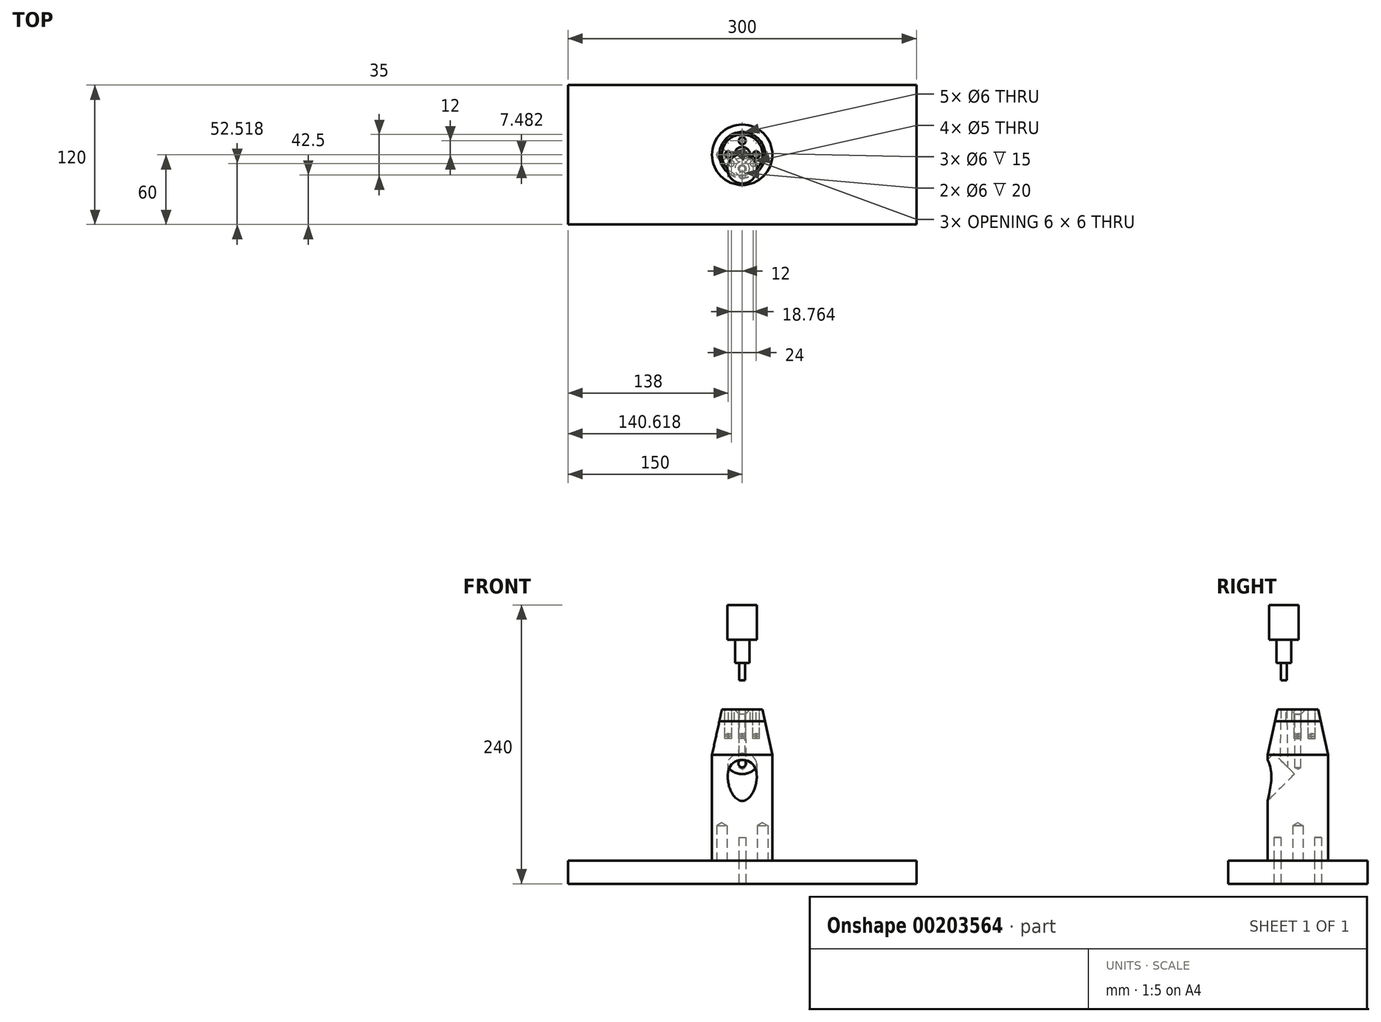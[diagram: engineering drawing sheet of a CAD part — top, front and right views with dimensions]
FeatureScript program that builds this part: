
annotation { "Feature Type Name" : "Feature", "Feature Type Description" : "" }
export const myFeature = defineFeature(function(context is Context, id is Id, definition is map)
    precondition{}
    {
        {
            var Q0;
            Q0=qCreatedBy(makeId("Front.planeOp"),FACE);
            var sketch = newSketch(context, id + "F0", { "sketchPlane" : qUnion([Q0])});
            skLineSegment(sketch, "E0", {"start": v(0, 0) * mm, "end": v(17.5, 0) * mm, "construction": true});
            skLineSegment(sketch, "E1", {"start": v(17.5, 0) * mm, "end": v(26, -39.09) * mm, "construction": true});
            skLineSegment(sketch, "E2", {"start": v(26, -39.09) * mm, "end": v(0, -39.09) * mm, "construction": true});
            skLineSegment(sketch, "E3", {"start": v(0, -10) * mm, "end": v(19.67, -10) * mm});
            skLineSegment(sketch, "E4", {"start": v(19.67, -10) * mm, "end": v(26, -39.09) * mm});
            skLineSegment(sketch, "E5", {"start": v(26, -130) * mm, "end": v(0, -130) * mm});
            skLineSegment(sketch, "E6", {"start": v(26, -39.09) * mm, "end": v(26, -130) * mm});
            skLineSegment(sketch, "E7", {"start": v(0, -130) * mm, "end": v(0, -10) * mm});
            skSolve(sketch);
        }
        {
            var Q0;
            Q0 = qSketchRegion(id + "F0", true);
            var Q1;
            Q1=sQuery(id+"F0.wireOp",EDGE,"E7");
            revolve(context, id + "F1", {"entities" : qUnion([Q0]), "axis" : qUnion([Q1]), "revolveType" : RevolveType.FULL});
        }
        {
            var Q0;
            Q0=qCreatedBy(makeId("Front.planeOp"),FACE);
            var sketch = newSketch(context, id + "F2", { "sketchPlane" : qUnion([Q0])});
            skPoint(sketch, "E8.0", {"position": v(0, 0) * mm});
            skLineSegment(sketch, "E9.0", {"start": v(0, 0) * mm, "end": v(17.5, 0) * mm});
            skLineSegment(sketch, "E10.0", {"start": v(17.5, 0) * mm, "end": v(19.67, -10) * mm});
            skLineSegment(sketch, "E11.0", {"start": v(0, -10) * mm, "end": v(19.67, -10) * mm});
            skLineSegment(sketch, "E12", {"start": v(0, -10) * mm, "end": v(0, 0) * mm});
            skPoint(sketch, "E13.orphan", {"position": v(26, -39.09) * mm});
            skSolve(sketch);
        }
        {
            var Q0;
            Q0 = qSketchRegion(id + "F2", true);
            var Q1;
            Q1=sQuery(id+"F2.wireOp",EDGE,"E12");
            revolve(context, id + "F3", {"entities" : qUnion([Q0]), "axis" : qUnion([Q1]), "revolveType" : RevolveType.FULL});
        }
        {
            var Q0;
            Q0=makeQuery(id+"F3.opRevolve","SWEPT_FACE",FACE,{"disambiguationData":[OSD([sQuery(id+"F2.wireOp",EDGE,"E9.0")])]});
            var sketch = newSketch(context, id + "F4", { "sketchPlane" : qUnion([Q0])});
            skCircle(sketch, "E14", {"center": v(0, 0) * mm, "radius": 12 * mm, "construction": true});
            skLineSegment(sketch, "E15", {"start": v(0, 0) * mm, "end": v(0, -17.5) * mm, "construction": true});
            skCircle(sketch, "E16", {"center": v(0, -12) * mm, "radius": 2.5 * mm});
            skSolve(sketch);
        }
        {
            var Q0;
            Q0 = qSketchRegion(id + "F4", true);
            extrude(context, id + "F5", {"entities" : qUnion([Q0]), "operationType" : NewBodyOperationType.REMOVE, "oppositeDirection" : true, "depth" : 50 * mm, "hasDraft" : true, "draftAngle" : 1 * degree});
        }
        {
            var Q0;
            Q0=makeQuery(id+"F3.opRevolve","SWEPT_FACE",FACE,{"disambiguationData":[OSD([sQuery(id+"F2.wireOp",EDGE,"E9.0")])]});
            var sketch = newSketch(context, id + "F6", { "sketchPlane" : qUnion([Q0])});
            skCircle(sketch, "E17.0", {"center": v(0, 0) * mm, "radius": 12 * mm, "construction": true});
            skLineSegment(sketch, "E18.0", {"start": v(0, 0) * mm, "end": v(0, -17.5) * mm, "construction": true});
            skLineSegment(sketch, "E19", {"start": v(0, 0) * mm, "end": v(-13.68, -10.91) * mm, "construction": true});
            skLineSegment(sketch, "E20", {"start": v(0, 0) * mm, "end": v(13.68, -10.91) * mm, "construction": true});
            skCircle(sketch, "E21", {"center": v(-9.38, -7.48) * mm, "radius": 2.5 * mm});
            skCircle(sketch, "E22", {"center": v(9.38, -7.48) * mm, "radius": 2.5 * mm});
            skSolve(sketch);
        }
        {
            var Q0;
            Q0 = qSketchRegion(id + "F6", true);
            extrude(context, id + "F7", {"entities" : qUnion([Q0]), "operationType" : NewBodyOperationType.REMOVE, "endBound" : BoundingType.UP_TO_NEXT, "oppositeDirection" : true, "depth" : 25 * mm});
        }
        {
            var Q0;
            Q0=makeQuery(id+"F4.imprint","IMPRINT",FACE,{"disambiguationData":[TD([[makeQuery(id+"F4.imprint","IMPRINT",EDGE,{"derivedFrom":sQuery(id+"F4.wireOp",EDGE,"E16")}),-1.0]])]});
            var sketch = newSketch(context, id + "F8", { "sketchPlane" : qUnion([Q0])});
            skCircle(sketch, "E23.0", {"center": v(0, 0) * mm, "radius": 12 * mm, "construction": true});
            skLineSegment(sketch, "E24", {"start": v(-17.5, 0) * mm, "end": v(17.5, 0) * mm, "construction": true});
            skCircle(sketch, "E25", {"center": v(-12, 0) * mm, "radius": 3 * mm});
            skCircle(sketch, "E26", {"center": v(12, 0) * mm, "radius": 3 * mm});
            skCircle(sketch, "E27", {"center": v(0, 12) * mm, "radius": 3 * mm});
            skSolve(sketch);
        }
        {
            var Q0;
            Q0 = qSketchRegion(id + "F8", true);
            extrude(context, id + "F9", {"entities" : qUnion([Q0]), "operationType" : NewBodyOperationType.REMOVE, "oppositeDirection" : true, "depth" : 25 * mm});
        }
        {
            var Q0;
            Q0 = qSketchRegion(id + "F8", true);
            extrude(context, id + "F10", {"entities" : qUnion([Q0]), "oppositeDirection" : true, "depth" : 25 * mm});
        }
        {
            var Q0;
            Q0=makeQuery(id+"F10.opExtrude","CAP_EDGE",EDGE,{"disambiguationData":[OSD([sQuery(id+"F8.wireOp",EDGE,"E25")])],"isStart":true});
            var Q1;
            Q1=makeQuery(id+"F10.opExtrude","CAP_EDGE",EDGE,{"disambiguationData":[OSD([sQuery(id+"F8.wireOp",EDGE,"E27")])],"isStart":true});
            var Q2;
            Q2=makeQuery(id+"F10.opExtrude","CAP_EDGE",EDGE,{"disambiguationData":[OSD([sQuery(id+"F8.wireOp",EDGE,"E26")])],"isStart":true});
            var Q3;
            Q3=makeQuery(id+"F10.opExtrude","CAP_EDGE",EDGE,{"disambiguationData":[OSD([sQuery(id+"F8.wireOp",EDGE,"E27")])],"isStart":false});
            var Q4;
            Q4=makeQuery(id+"F10.opExtrude","CAP_EDGE",EDGE,{"disambiguationData":[OSD([sQuery(id+"F8.wireOp",EDGE,"E25")])],"isStart":false});
            var Q5;
            Q5=makeQuery(id+"F10.opExtrude","CAP_EDGE",EDGE,{"disambiguationData":[OSD([sQuery(id+"F8.wireOp",EDGE,"E26")])],"isStart":false});
            fillet(context, id + "F11", {"entities" : qUnion([Q0, Q1, Q2, Q3, Q4, Q5]), "radius" : 2 * mm, "tangentPropagation" : true, "allowEdgeOverflow" : false});
        }
        {
            var Q0;
            Q0=sQuery(id+"F4.wireOp",VERTEX,"E14.center");
            var Q1;
            Q1=makeQuery(id+"F1.opRevolve","SWEPT_BODY",BODY,{"disambiguationData":[OSD([sQuery(id+"F0.wireOp",EDGE,"E3"),sQuery(id+"F0.wireOp",EDGE,"E4"),sQuery(id+"F0.wireOp",EDGE,"E5"),sQuery(id+"F0.wireOp",EDGE,"E6"),sQuery(id+"F0.wireOp",EDGE,"E7")])]});
            var Q2;
            Q2=makeQuery(id+"F3.opRevolve","SWEPT_BODY",BODY,{"disambiguationData":[OSD([sQuery(id+"F2.wireOp",EDGE,"E9.0"),sQuery(id+"F2.wireOp",EDGE,"E10.0"),sQuery(id+"F2.wireOp",EDGE,"E11.0"),sQuery(id+"F2.wireOp",EDGE,"E12")])]});
            hole(context, id + "F12", {"style" : HoleStyle.C_SINK, "endStyle" : HoleEndStyle.BLIND, "standardTappedOrClearance" : lookupTablePath({ "standard" : "ISO", "engagement" : "75%", "pitch" : "1 mm", "size" : "M6", "type" : "Tapped" }), "standardBlindInLast" : lookupTablePath({ "standard" : "ISO", "engagement" : "75%", "pitch" : "1 mm", "size" : "M6", "type" : "Tapped" }), "holeDiameter" : 5 * mm, "cSinkDiameter" : 13.44 * mm, "cSinkAngle" : 90 * degree, "holeDepth" : 50 * mm, "startFromSketch" : true, "locations" : qUnion([Q0]), "scope" : qUnion([Q1, Q2]), "majorDiameter" : 6 * mm});
        }
        {
            var Q0;
            Q0=qCreatedBy(makeId("Right.planeOp"),FACE);
            var sketch = newSketch(context, id + "F13", { "sketchPlane" : qUnion([Q0])});
            skLineSegment(sketch, "E28", {"start": v(0, -35) * mm, "end": v(-36.42, -71.42) * mm, "construction": true});
            skSolve(sketch);
        }
        {
            var Q0;
            Q0=sQuery(id+"F13.wireOp",EDGE,"E28");
            var Q1;
            Q1=sQuery(id+"F13.wireOp",VERTEX,"E28.end");
            cPlane(context, id + "F14", {"entities" : qUnion([Q0, Q1]), "cplaneType" : CPlaneType.LINE_POINT, "offset" : 25 * mm, "width" : 150 * mm, "height" : 150 * mm});
        }
        {
            var Q0;
            Q0=qCreatedBy(id+"F14.planeOp",FACE);
            var sketch = newSketch(context, id + "F15", { "sketchPlane" : qUnion([Q0])});
            skPoint(sketch, "E29.0", {"position": v(0, -24.75) * mm});
            skCircle(sketch, "E30", {"center": v(0, -24.75) * mm, "radius": 12.5 * mm});
            skSolve(sketch);
        }
        {
            var Q0;
            Q0 = qSketchRegion(id + "F15", true);
            extrude(context, id + "F16", {"entities" : qUnion([Q0]), "operationType" : NewBodyOperationType.REMOVE, "oppositeDirection" : true, "depth" : 35 * mm});
        }
        {
            var Q0;
            Q0=qCreatedBy(makeId("Top.planeOp"),FACE);
            cPlane(context, id + "F17", {"entities" : qUnion([Q0]), "cplaneType" : CPlaneType.OFFSET, "offset" : 25 * mm, "width" : 150 * mm, "height" : 150 * mm});
        }
        {
            var Q0;
            Q0=qCreatedBy(id+"F17.planeOp",FACE);
            var sketch = newSketch(context, id + "F18", { "sketchPlane" : qUnion([Q0])});
            skCircle(sketch, "E31.0", {"center": v(0, -12) * mm, "radius": 2.5 * mm});
            skSolve(sketch);
        }
        {
            var Q0;
            Q0 = qSketchRegion(id + "F18", true);
            extrude(context, id + "F19", {"entities" : qUnion([Q0]), "depth" : 15 * mm});
        }
        {
            var Q0;
            Q0=makeQuery(id+"F19.opExtrude","CAP_FACE",FACE,{"disambiguationData":[OSD([sQuery(id+"F18.wireOp",EDGE,"E31.0")])],"isStart":false});
            var sketch = newSketch(context, id + "F20", { "sketchPlane" : qUnion([Q0])});
            skCircle(sketch, "E32", {"center": v(0, -12) * mm, "radius": 6.25 * mm});
            skSolve(sketch);
        }
        {
            var Q0;
            Q0 = qSketchRegion(id + "F20", true);
            extrude(context, id + "F21", {"entities" : qUnion([Q0]), "operationType" : NewBodyOperationType.ADD, "depth" : 20 * mm});
        }
        {
            var Q0;
            Q0=makeQuery(id+"F21.opExtrude","CAP_FACE",FACE,{"disambiguationData":[OSD([sQuery(id+"F20.wireOp",EDGE,"E32")])],"isStart":false});
            var sketch = newSketch(context, id + "F22", { "sketchPlane" : qUnion([Q0])});
            skCircle(sketch, "E33", {"center": v(0, -12) * mm, "radius": 12.7 * mm});
            skSolve(sketch);
        }
        {
            var Q0;
            Q0 = qSketchRegion(id + "F22", true);
            extrude(context, id + "F23", {"entities" : qUnion([Q0]), "operationType" : NewBodyOperationType.ADD, "depth" : 30 * mm});
        }
        {
            var Q0;
            Q0=makeQuery(id+"F1.opRevolve","SWEPT_FACE",FACE,{"disambiguationData":[OSD([sQuery(id+"F0.wireOp",EDGE,"E5")])]});
            var sketch = newSketch(context, id + "F24", { "sketchPlane" : qUnion([Q0])});
            skPoint(sketch, "E34.0", {"position": v(0, 0) * mm});
            skLineSegment(sketch, "E35.bottom", {"start": v(-150, -60) * mm, "end": v(150, -60) * mm});
            skLineSegment(sketch, "E35.top", {"start": v(-150, 60) * mm, "end": v(150, 60) * mm});
            skLineSegment(sketch, "E35.left", {"start": v(-150, -60) * mm, "end": v(-150, 60) * mm});
            skLineSegment(sketch, "E35.right", {"start": v(150, -60) * mm, "end": v(150, 60) * mm});
            skSolve(sketch);
        }
        {
            var Q0;
            Q0 = qSketchRegion(id + "F24", true);
            extrude(context, id + "F25", {"entities" : qUnion([Q0]), "depth" : 20 * mm});
        }
        {
            var Q0;
            Q0=makeQuery(id+"F25.opExtrude","CAP_FACE",FACE,{"disambiguationData":[OSD([sQuery(id+"F24.wireOp",EDGE,"E35.bottom"),sQuery(id+"F24.wireOp",EDGE,"E35.top"),sQuery(id+"F24.wireOp",EDGE,"E35.left"),sQuery(id+"F24.wireOp",EDGE,"E35.right")])],"isStart":false});
            var sketch = newSketch(context, id + "F26", { "sketchPlane" : qUnion([Q0])});
            skPoint(sketch, "E36.0", {"position": v(0, 0) * mm});
            skCircle(sketch, "E37", {"center": v(0, 0) * mm, "radius": 17.5 * mm, "construction": true});
            skLineSegment(sketch, "E38", {"start": v(0, 17.5) * mm, "end": v(0, -17.5) * mm, "construction": true});
            skLineSegment(sketch, "E39", {"start": v(17.5, 0) * mm, "end": v(-17.5, 0) * mm, "construction": true});
            skPoint(sketch, "E40", {"position": v(-17.5, 0) * mm});
            skPoint(sketch, "E41", {"position": v(17.5, 0) * mm});
            skCircle(sketch, "E42", {"center": v(0, 17.5) * mm, "radius": 3 * mm});
            skCircle(sketch, "E43", {"center": v(0, -17.5) * mm, "radius": 3 * mm});
            skSolve(sketch);
        }
        {
            var Q0;
            Q0 = qSketchRegion(id + "F26", true);
            extrude(context, id + "F27", {"entities" : qUnion([Q0]), "operationType" : NewBodyOperationType.REMOVE, "oppositeDirection" : true, "depth" : 40 * mm});
        }
        {
            var Q0;
            Q0=sQuery(id+"F26.wireOp",VERTEX,"E40");
            var Q1;
            Q1=sQuery(id+"F26.wireOp",VERTEX,"E41");
            var Q2;
            Q2=makeQuery(id+"F1.opRevolve","SWEPT_BODY",BODY,{"disambiguationData":[OSD([sQuery(id+"F0.wireOp",EDGE,"E3"),sQuery(id+"F0.wireOp",EDGE,"E4"),sQuery(id+"F0.wireOp",EDGE,"E5"),sQuery(id+"F0.wireOp",EDGE,"E6"),sQuery(id+"F0.wireOp",EDGE,"E7")])]});
            hole(context, id + "F28", {"style" : HoleStyle.C_BORE, "endStyle" : HoleEndStyle.BLIND, "standardTappedOrClearance" : lookupTablePath({ "standard" : "ISO", "engagement" : "75%", "pitch" : "1 mm", "size" : "M10", "type" : "Tapped" }), "standardBlindInLast" : lookupTablePath({ "standard" : "ISO", "engagement" : "75%", "pitch" : "1 mm", "size" : "M10", "type" : "Tapped" }), "holeDiameter" : 9 * mm, "cBoreDiameter" : 17.25 * mm, "cBoreDepth" : 10 * mm, "holeDepth" : 50 * mm, "startFromSketch" : true, "locations" : qUnion([Q0, Q1]), "scope" : qUnion([Q2]), "majorDiameter" : 10 * mm});
        }
    });
